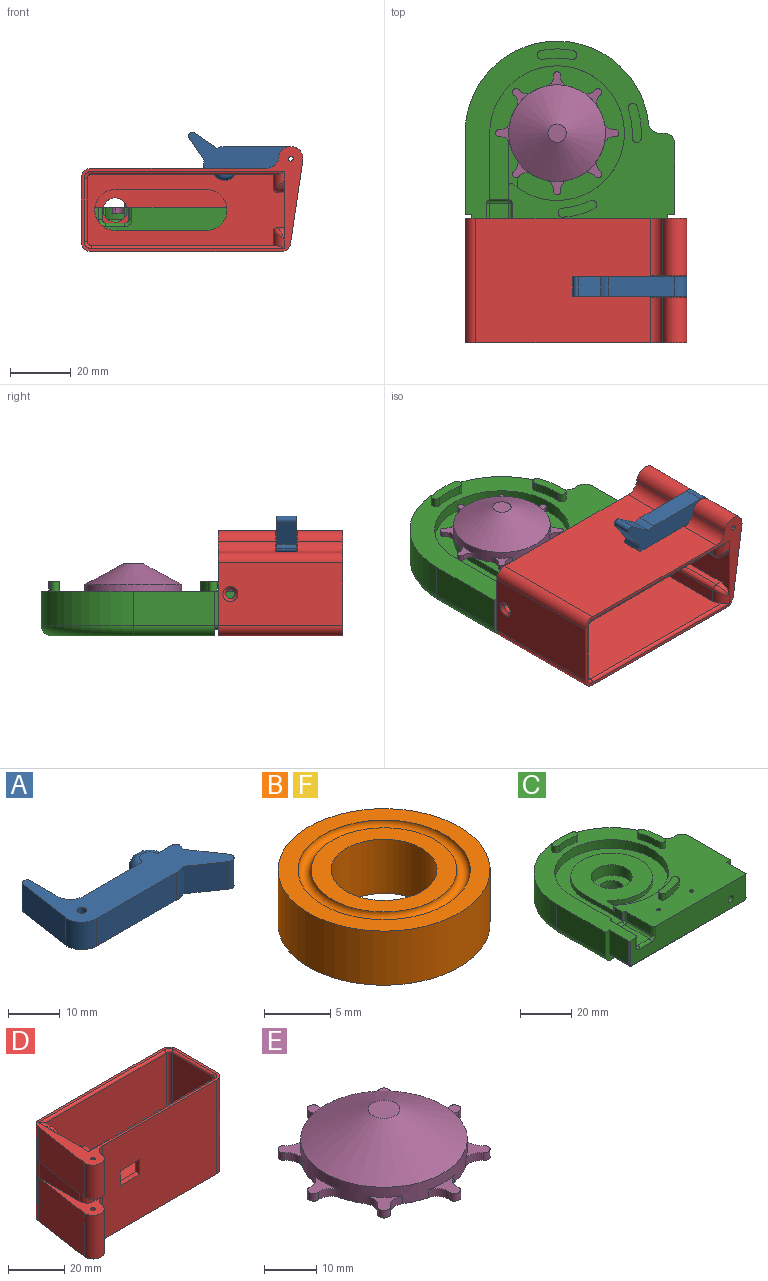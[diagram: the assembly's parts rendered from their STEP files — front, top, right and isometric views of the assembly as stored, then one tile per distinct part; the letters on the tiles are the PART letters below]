
ASSEMBLY  parts=6 mates=9
PART A: 20 faces, bbox 37.6x23.8x6.5 mm
  f0: plane 37.63x23.77mm, normal (0,0,1), area 292.8mm2, adj f1,f2,f3,f4,f5,f6,f7,f8
  f1: plane 13.58x6.5mm, normal (-0.99,0.15,0), area 89.3mm2, adj f0,f2,f12,f17
  f2: cylinder r=4mm len=6.5mm, axis (0,0,-1), area 44.7mm2, adj f0,f1,f3,f12
  f3: plane 21.75x6.5mm, normal (0,-1,0), area 141.4mm2, adj f0,f2,f4,f12
  f4: cylinder r=7.13mm len=6.5mm, axis (0,0,-1), area 17.3mm2, adj f0,f3,f5,f12
  f5: plane 7.29x6.5mm, normal (-0.57,-0.82,0), area 57.5mm2, adj f0,f4,f6,f12
  f6: cylinder r=1.27mm len=6.5mm, axis (0,0,-1), area 22.9mm2, adj f0,f5,f7,f12
  f7: plane 7.29x6.5mm, normal (0.82,0.57,0), area 57.5mm2, adj f0,f6,f8,f12
  f8: cylinder r=7.13mm len=6.5mm, axis (0,0,-1), area 9.7mm2, adj f0,f7,f9,f12
  f9: cylinder r=1mm len=6.5mm, axis (0,0,-1), area 11.3mm2, adj f0,f8,f10,f12
  f10: plane 6.5x4.05mm, normal (0,1,0), area 15mm2, adj f0,f9,f11,f12,f18,f19
  f11: cylinder r=4mm len=8mm, axis (0,0,-1), area 31.4mm2, adj f10,f14,f18,f19
  f12: plane 37.63x23.77mm, normal (0,0,-1), area 292.8mm2, adj f1,f2,f3,f4,f5,f6,f7,f8
  f13: cylinder r=0.95mm len=6.5mm, axis (0,0,-1), area 38.9mm2, adj f0,f12
  f14: plane 16.25x6.5mm, normal (0,1,0), area 94.3mm2, adj f0,f11,f12,f16,f18,f19
  f15: plane 6.88x6.5mm, normal (1,0,0), area 44.7mm2, adj f0,f12,f16,f17
  f16: cylinder r=3.5mm len=6.5mm, axis (0,0,-1), area 39.1mm2, adj f0,f12,f14,f15
  f17: cylinder r=1mm len=6.5mm, axis (0,0,1), area 19.5mm2, adj f0,f1,f12,f15
  f18: torus R=2mm, axis (0,0,1), area 32.3mm2, adj f0,f10,f11,f14
  f19: torus R=2mm, axis (0,0,1), area 32.3mm2, adj f10,f11,f12,f14
PART B: 8 faces, bbox 16x16x5.7 mm
  f0: plane 16x16mm, normal (0,0,1), area 68.3mm2, adj f2,f4
  f1: plane 16x16mm, normal (0,0,-1), area 68.3mm2, adj f2,f3
  f2: cylinder r=8mm len=16mm, axis (0,0,-1), area 251.3mm2, adj f0,f1
  f3: torus R=6mm, axis (0,0,-1), area 59.2mm2, adj f1,f7
  f4: torus R=6mm, axis (0,0,-1), area 59.2mm2, adj f0,f5
  f5: plane 11x11mm, normal (0,0,1), area 44.8mm2, adj f4,f6
  f6: cylinder r=4mm len=8mm, axis (0,0,-1), area 125.7mm2, adj f5,f7
  f7: plane 11x11mm, normal (0,0,-1), area 44.8mm2, adj f3,f6
PART C: 75 faces, bbox 71.5x70.6x17.8 mm
  f0: plane 69x68.06mm, normal (0,0,1), area 2131.6mm2, adj f2,f3,f5,f6,f10,f16,f19,f20
  f1: plane 62x53.56mm, normal (0,0,-1), area 2566mm2, adj f15,f21,f24,f26,f27,f28,f42
  f2: plane 23.28x11.25mm, normal (1,0,0), area 261.9mm2, adj f0,f21,f22,f42
  f3: plane 11.25x1.62mm, normal (0,1,0), area 18.2mm2, adj f0,f22,f24,f25
  f4: plane 44.31x44.31mm, normal (0,0,1), area 787.6mm2, adj f5,f6,f8,f9,f10,f17,f18,f51
  f5: plane 21.96x4.13mm, normal (-1,0,0), area 56mm2, adj f0,f4,f8,f11,f16,f48
  f6: plane 21.96x4.13mm, normal (1,0,0), area 90.6mm2, adj f0,f4,f10,f50
  f7: cylinder r=4.5mm len=9mm, axis (0,0,1), area 77.8mm2, adj f13,f14
  f8: cylinder r=15.91mm len=31.81mm, axis (0,0,1), area 187.3mm2, adj f4,f5,f11,f18
  f9: plane 6.16x2.13mm, normal (1,0,0), area 13.1mm2, adj f4,f11,f17,f18
  f10: cylinder r=22.16mm len=44.31mm, axis (0,0,1), area 491.4mm2, adj f0,f4,f6,f11,f16,f17
  f11: plane 34.01x31.81mm, normal (0,0,1), area 625.2mm2, adj f5,f8,f9,f10,f12,f16,f17,f18
  f12: cylinder r=8mm len=16mm, axis (0,0,1), area 251.3mm2, adj f11,f13
  f13: plane 16x16mm, normal (0,0,1), area 137.4mm2, adj f7,f12
  f14: plane 16x16mm, normal (0,0,-1), area 137.4mm2, adj f7,f15
  f15: cylinder r=8mm len=16mm, axis (0,0,-1), area 251.3mm2, adj f1,f14
  f16: cylinder r=0.8mm len=2mm, axis (0,0,1), area 3.7mm2, adj f0,f5,f10,f11
  f17: cylinder r=0.8mm len=2.13mm, axis (0,0,1), area 1.6mm2, adj f4,f9,f10,f11
  f18: cylinder r=0.8mm len=2.13mm, axis (0,0,1), area 4.1mm2, adj f4,f8,f9,f11
  f19: plane 26.78x11.25mm, normal (-1,0,0), area 301.3mm2, adj f0,f20,f27,f42
  f20: cylinder r=30.28mm len=60.4mm, axis (0,0,1), area 1034.9mm2, adj f0,f19,f25,f28
  f21: cylinder r=3.5mm len=23.28mm, axis (0,1,0), area 128mm2, adj f1,f2,f23,f42
  f22: cylinder r=3.5mm len=11.25mm, axis (0,0,-1), area 61.9mm2, adj f0,f2,f3,f23
  f23: sphere r=3.5mm, area 19.2mm2, adj f21,f22,f24
  f24: cylinder r=3.5mm len=3.5mm, axis (1,0,0), area 8.9mm2, adj f1,f3,f23,f26
  f25: cylinder r=3.5mm len=11.25mm, axis (0,0,1), area 57.8mm2, adj f0,f3,f20,f26
  f26: torus R=7mm, axis (0,0,1), area 38.5mm2, adj f1,f24,f25,f28
  f27: cylinder r=3.5mm len=26.78mm, axis (0,1,0), area 147.2mm2, adj f1,f19,f28,f42
  f28: torus R=26.78mm, axis (0,0,1), area 484.5mm2, adj f1,f20,f26,f27
  f29: plane 63.7x12.1mm, normal (0,-1,0), area 694.9mm2, adj f0,f36,f37,f38,f39,f40,f41,f53
  f30: plane 11.25x10.6mm, normal (1,0,0), area 119.3mm2, adj f0,f34,f41,f42
  f31: plane 11.25x10.6mm, normal (-1,0,0), area 119.3mm2, adj f0,f32,f37,f42
  f32: cylinder r=1.25mm len=10.6mm, axis (0,1,0), area 20.8mm2, adj f31,f33,f38,f42
  f33: plane 62x10.6mm, normal (0,0,-1), area 653.2mm2, adj f32,f34,f39,f42,f43,f44
  f34: cylinder r=1.25mm len=10.6mm, axis (0,1,0), area 20.8mm2, adj f30,f33,f40,f42
  f35: plane 3x3mm, normal (0,-1,0), area 7.1mm2, adj f36
  f36: cylinder r=1.5mm len=12mm, axis (0,-1,0), area 113.1mm2, adj f29,f35
  f37: cylinder r=0.4mm len=11.25mm, axis (0,0,1), area 7.1mm2, adj f0,f29,f31,f38
  f38: torus R=0.85mm, axis (0,1,0), area 1.1mm2, adj f29,f32,f37,f39
  f39: cylinder r=0.4mm len=62mm, axis (-1,0,0), area 39mm2, adj f29,f33,f38,f40
  f40: torus R=0.85mm, axis (0,1,0), area 1.1mm2, adj f29,f34,f39,f41
  f41: cylinder r=0.4mm len=11.25mm, axis (0,0,-1), area 7.1mm2, adj f0,f29,f30,f40
  f42: plane 69x14.75mm, normal (0,-1,0), area 206.9mm2, adj f0,f1,f2,f19,f21,f27,f30,f31
  f43: cylinder r=0.79mm len=12.5mm, axis (0,0,-1), area 62.3mm2, adj f0,f33
  f44: cylinder r=0.79mm len=12.5mm, axis (0,0,-1), area 62.3mm2, adj f0,f33
  f45: plane 13.48x4.13mm, normal (1,0,0), area 55.6mm2, adj f0,f50,f56,f59
  f46: plane 13.48x6.25mm, normal (0,0,1), area 84.2mm2, adj f51,f52,f56,f57
  f47: plane 13.48x4.13mm, normal (-1,0,0), area 55.6mm2, adj f0,f48,f52,f53
  f48: cylinder r=1.18mm len=4.13mm, axis (0,0,-1), area 7.6mm2, adj f0,f5,f47,f49
  f49: sphere r=1.18mm, area 2.2mm2, adj f48,f51,f52
  f50: cylinder r=1.18mm len=4.13mm, axis (0,0,1), area 7.6mm2, adj f0,f6,f45,f54
  f51: cylinder r=1.18mm len=6.25mm, axis (-1,0,0), area 11.5mm2, adj f4,f46,f49,f54
  f52: cylinder r=1.18mm len=13.48mm, axis (0,-1,0), area 24.9mm2, adj f46,f47,f49,f55
  f53: cylinder r=1.18mm len=4.13mm, axis (0,0,1), area 7.6mm2, adj f0,f29,f47,f55
  f54: sphere r=1.18mm, area 2.2mm2, adj f50,f51,f56
  f55: torus R=2.35mm, axis (0,1,0), area 4.6mm2, adj f29,f52,f53,f57
  f56: cylinder r=1.18mm len=13.48mm, axis (0,1,0), area 24.9mm2, adj f45,f46,f54,f58
  f57: cylinder r=1.18mm len=6.25mm, axis (1,0,0), area 11.5mm2, adj f29,f46,f55,f58
  f58: torus R=2.35mm, axis (0,1,0), area 4.6mm2, adj f29,f56,f57,f59
  f59: cylinder r=1.18mm len=4.13mm, axis (0,0,-1), area 7.6mm2, adj f0,f29,f45,f58
  f60: cylinder r=24.72mm len=9.43mm, axis (0,0,-1), area 28.5mm2, adj f0,f61,f63,f64
  f61: cylinder r=1.5mm len=3mm, axis (0,0,-1), area 14.1mm2, adj f0,f60,f62,f64
  f62: cylinder r=27.72mm len=10.57mm, axis (0,0,-1), area 31.9mm2, adj f0,f61,f63,f64
  f63: cylinder r=1.5mm len=3mm, axis (0,0,-1), area 14.1mm2, adj f0,f60,f62,f64
  f64: plane 13x3.48mm, normal (0,0,1), area 37.3mm2, adj f60,f61,f62,f63
  f65: cylinder r=24.72mm len=9.35mm, axis (0,0,-1), area 28.5mm2, adj f0,f66,f68,f69
  f66: cylinder r=1.5mm len=3mm, axis (0,0,-1), area 14.1mm2, adj f0,f65,f67,f69
  f67: cylinder r=27.72mm len=10.48mm, axis (0,0,-1), area 31.9mm2, adj f0,f66,f68,f69
  f68: cylinder r=1.5mm len=3mm, axis (0,0,-1), area 14.1mm2, adj f0,f65,f67,f69
  f69: plane 12.91x4.35mm, normal (0,0,1), area 37.3mm2, adj f65,f66,f67,f68
  f70: cylinder r=24.72mm len=9.11mm, axis (0,0,-1), area 28.5mm2, adj f0,f71,f73,f74
  f71: cylinder r=1.5mm len=3mm, axis (0,0,-1), area 14.1mm2, adj f0,f70,f72,f74
  f72: cylinder r=27.72mm len=10.21mm, axis (0,0,-1), area 31.9mm2, adj f0,f71,f73,f74
  f73: cylinder r=1.5mm len=3mm, axis (0,0,-1), area 14.1mm2, adj f0,f70,f72,f74
  f74: plane 12.66x5.59mm, normal (0,0,1), area 37.3mm2, adj f70,f71,f72,f73
PART D: 56 faces, bbox 73x34.6x41 mm
  f0: plane 27.06x19mm, normal (-0.99,0.15,0), area 519.7mm2, adj f2,f6,f47,f55
  f1: cylinder r=4mm len=19mm, axis (0,0,-1), area 111.1mm2, adj f2,f5,f47,f55
  f2: cylinder r=4mm len=19mm, axis (0,0,-1), area 241.6mm2, adj f0,f1,f47,f55
  f3: cylinder r=0.79mm len=19mm, axis (0,0,-1), area 94.8mm2, adj f47,f55
  f4: cylinder r=0.79mm len=15mm, axis (0,0,-1), area 74.8mm2, adj f25,f54
  f5: plane 62x41mm, normal (0,-1,0), area 2325.6mm2, adj f1,f9,f10,f25,f31,f32,f33,f34
  f6: cylinder r=3.5mm len=41mm, axis (0,0,-1), area 208mm2, adj f0,f8,f13,f25,f47,f52,f54,f55
  f7: plane 60.95x29mm, normal (0,1,0), area 1668.8mm2, adj f21,f22,f26,f31,f32,f33,f34,f37
  f8: plane 20.5x7mm, normal (-1,0,0), area 143.5mm2, adj f6,f9,f54,f55
  f9: cylinder r=3.5mm len=7mm, axis (0,0,-1), area 38.5mm2, adj f5,f8,f54,f55
  f10: cylinder r=3.5mm len=41mm, axis (0,0,-1), area 225.4mm2, adj f5,f11,f25,f47
  f11: plane 41x20.5mm, normal (1,0,0), area 821.6mm2, adj f10,f12,f25,f47,f53
  f12: cylinder r=3.5mm len=41mm, axis (0,0,-1), area 225.4mm2, adj f11,f13,f25,f47
  f13: plane 62x41mm, normal (0,1,0), area 2542mm2, adj f6,f12,f25,f47
  f14: plane 30x19mm, normal (1,0,0), area 351mm2, adj f15,f24,f25,f26,f35,f38
  f15: plane 26.25x2.25mm, normal (0,-1,0), area 59.1mm2, adj f14,f16,f26,f38
  f16: cylinder r=1.5mm len=26.25mm, axis (0,0,-1), area 61.9mm2, adj f15,f17,f26,f39
  f17: plane 26.25x4.5mm, normal (1,0,0), area 118.1mm2, adj f16,f18,f26,f40
  f18: plane 60.95x29mm, normal (0,-1,0), area 1733.8mm2, adj f17,f19,f26,f40,f45
  f19: cylinder r=1.5mm len=29mm, axis (0,0,-1), area 68.3mm2, adj f18,f20,f26,f44
  f20: plane 29x20.5mm, normal (-1,0,0), area 594.5mm2, adj f19,f21,f26,f43
  f21: cylinder r=1.5mm len=29mm, axis (0,0,-1), area 68.3mm2, adj f7,f20,f26,f42
  f22: plane 26.25x4.5mm, normal (1,0,0), area 118.1mm2, adj f7,f23,f26,f37
  f23: cylinder r=1.5mm len=26.25mm, axis (0,0,-1), area 61.9mm2, adj f22,f24,f26,f36
  f24: plane 26.25x2.25mm, normal (0,1,0), area 59.1mm2, adj f14,f23,f26,f35
  f25: plane 73x34.63mm, normal (0,0,1), area 303.6mm2, adj f4,f5,f6,f10,f11,f12,f13,f14
  f26: plane 65x23.5mm, normal (0,0,1), area 934.4mm2, adj f7,f14,f15,f16,f17,f18,f19,f20
  f27: cylinder r=6.75mm len=13.5mm, axis (0,0,1), area 63.6mm2, adj f26,f28,f30,f46
  f28: plane 30x3mm, normal (0,-1,0), area 90mm2, adj f26,f27,f29,f46
  f29: cylinder r=6.75mm len=13.5mm, axis (0,0,1), area 63.6mm2, adj f26,f28,f30,f46
  f30: plane 30x3mm, normal (0,1,0), area 90mm2, adj f26,f27,f29,f46
  f31: plane 10x2mm, normal (0,0,1), area 20mm2, adj f5,f7,f32,f33
  f32: plane 6.5x2mm, normal (1,0,0), area 13mm2, adj f5,f7,f31,f34
  f33: plane 6.5x2mm, normal (-1,0,0), area 13mm2, adj f5,f7,f31,f34
  f34: plane 10x2mm, normal (0,0,-1), area 20mm2, adj f5,f7,f32,f33
  f35: cylinder r=3.75mm len=3.75mm, axis (1,0,0), area 8.4mm2, adj f14,f24,f36
  f36: bspline ~4.43x3.75mm, area 9.4mm2, adj f23,f35,f37
  f37: cylinder r=3.75mm len=5.5mm, axis (0,-1,0), area 22.8mm2, adj f7,f22,f25,f36,f41
  f38: cylinder r=3.75mm len=3.75mm, axis (-1,0,0), area 8.4mm2, adj f14,f15,f39
  f39: bspline ~4.43x3.75mm, area 9.4mm2, adj f16,f38,f40
  f40: cylinder r=3.75mm len=5.5mm, axis (0,-1,0), area 22.8mm2, adj f17,f18,f25,f39,f45
  f41: cylinder r=1mm len=63.5mm, axis (1,0,0), area 97.6mm2, adj f7,f25,f37,f42
  f42: torus R=2.5mm, axis (0,0,1), area 4.6mm2, adj f21,f25,f41,f43
  f43: cylinder r=1mm len=20.5mm, axis (0,1,0), area 32.2mm2, adj f20,f25,f42,f44
  f44: torus R=2.5mm, axis (0,0,1), area 4.6mm2, adj f19,f25,f43,f45
  f45: cylinder r=1mm len=63.5mm, axis (-1,0,0), area 97.6mm2, adj f18,f25,f40,f44
  f46: plane 43.5x13.5mm, normal (0,0,1), area 497.9mm2, adj f27,f28,f29,f30,f48
  f47: plane 73x34.63mm, normal (0,0,-1), area 1933.7mm2, adj f0,f1,f2,f3,f5,f6,f10,f11
  f48: cylinder r=4mm len=8mm, axis (0,0,1), area 194.3mm2, adj f46,f47,f49
  f49: cylinder r=1.45mm len=6.52mm, axis (1,0,0), area 58.2mm2, adj f48,f53
  f50: cylinder r=4mm len=15mm, axis (0,0,-1), area 87.7mm2, adj f5,f25,f51,f54
  f51: cylinder r=4mm len=15mm, axis (0,0,-1), area 190.8mm2, adj f25,f50,f52,f54
  f52: plane 27.06x15mm, normal (-0.99,0.15,0), area 410.3mm2, adj f6,f25,f51,f54
  f53: cone r=1.45mm half-angle=45deg, axis (1,0,0), area 17.3mm2, adj f11,f49
  f54: plane 31.64x11.95mm, normal (0,0,-1), area 96.9mm2, adj f4,f5,f6,f8,f9,f50,f51,f52
  f55: plane 31.64x11.95mm, normal (0,0,1), area 96.9mm2, adj f0,f1,f2,f3,f5,f6,f8,f9
PART E: 42 faces, bbox 40.5x40.5x11.1 mm
  f0: plane 40.46x40.46mm, normal (0,0,-1), area 843.4mm2, adj f9,f10,f11,f12,f13,f14,f15,f16
  f1: plane 6.55x5.5mm, normal (-1,0,0), area 36mm2, adj f38,f39,f41
  f2: plane 6.24x6.24mm, normal (0,0,1), area 12.4mm2, adj f9,f16,f17,f18
  f3: plane 7.18x4.74mm, normal (0,0,1), area 12.4mm2, adj f9,f19,f20,f21
  f4: plane 6.24x6.24mm, normal (0,0,1), area 12.4mm2, adj f9,f22,f23,f24
  f5: plane 7.18x4.74mm, normal (0,0,1), area 12.4mm2, adj f9,f25,f26,f27
  f6: plane 6.24x6.24mm, normal (0,0,1), area 12.4mm2, adj f9,f28,f29,f30
  f7: plane 7.18x4.74mm, normal (0,0,1), area 12.4mm2, adj f9,f31,f32,f33
  f8: plane 7.18x4.74mm, normal (0,0,1), area 12.4mm2, adj f13,f14,f15,f35
  f9: cylinder r=15.91mm len=31.81mm, axis (0,0,-1), area 291.1mm2, adj f0,f2,f3,f4,f5,f6,f7,f10
  f10: cylinder r=3.12mm len=4.1mm, axis (0,0,-1), area 8.2mm2, adj f0,f9,f11,f34
  f11: cylinder r=1.2mm len=2.14mm, axis (0,0,-1), area 7.3mm2, adj f0,f10,f12,f34
  f12: cylinder r=3.12mm len=4.1mm, axis (0,0,-1), area 8.2mm2, adj f0,f9,f11,f34
  f13: cylinder r=3.12mm len=3.4mm, axis (0,0,-1), area 8.2mm2, adj f0,f8,f9,f14
  f14: cylinder r=1.2mm len=2.4mm, axis (0,0,-1), area 7.3mm2, adj f0,f8,f13,f15
  f15: cylinder r=3.12mm len=3.4mm, axis (0,0,-1), area 8.2mm2, adj f0,f8,f9,f14
  f16: cylinder r=3.12mm len=4.1mm, axis (0,0,-1), area 8.2mm2, adj f0,f2,f9,f17
  f17: cylinder r=1.2mm len=2.14mm, axis (0,0,-1), area 7.3mm2, adj f0,f2,f16,f18
  f18: cylinder r=3.12mm len=4.1mm, axis (0,0,-1), area 8.2mm2, adj f0,f2,f9,f17
  f19: cylinder r=3.12mm len=3.4mm, axis (0,0,-1), area 8.2mm2, adj f0,f3,f9,f20
  f20: cylinder r=1.2mm len=2.4mm, axis (0,0,-1), area 7.3mm2, adj f0,f3,f19,f21
  f21: cylinder r=3.12mm len=3.4mm, axis (0,0,-1), area 8.2mm2, adj f0,f3,f9,f20
  f22: cylinder r=3.12mm len=4.1mm, axis (0,0,-1), area 8.2mm2, adj f0,f4,f9,f23
  f23: cylinder r=1.2mm len=2.14mm, axis (0,0,-1), area 7.3mm2, adj f0,f4,f22,f24
  f24: cylinder r=3.12mm len=4.1mm, axis (0,0,-1), area 8.2mm2, adj f0,f4,f9,f23
  f25: cylinder r=3.12mm len=3.4mm, axis (0,0,-1), area 8.2mm2, adj f0,f5,f9,f26
  f26: cylinder r=1.2mm len=2.4mm, axis (0,0,-1), area 7.3mm2, adj f0,f5,f25,f27
  f27: cylinder r=3.12mm len=3.4mm, axis (0,0,-1), area 8.2mm2, adj f0,f5,f9,f26
  f28: cylinder r=3.12mm len=4.1mm, axis (0,0,-1), area 8.2mm2, adj f0,f6,f9,f29
  f29: cylinder r=1.2mm len=2.14mm, axis (0,0,-1), area 7.3mm2, adj f0,f6,f28,f30
  f30: cylinder r=3.12mm len=4.1mm, axis (0,0,-1), area 8.2mm2, adj f0,f6,f9,f29
  f31: cylinder r=3.12mm len=3.4mm, axis (0,0,-1), area 8.2mm2, adj f0,f7,f9,f32
  f32: cylinder r=1.2mm len=2.4mm, axis (0,0,-1), area 7.3mm2, adj f0,f7,f31,f33
  f33: cylinder r=3.12mm len=3.4mm, axis (0,0,-1), area 8.2mm2, adj f0,f7,f9,f32
  f34: plane 6.24x6.24mm, normal (0,0,1), area 12.4mm2, adj f9,f10,f11,f12
  f35: extruded ~7.18x2.33mm, area 16.8mm2, adj f8,f9,f37
  f36: plane 6x6mm, normal (0,0,1), area 28.3mm2, adj f37
  f37: cone r=3mm half-angle=61.5deg, axis (0,0,-1), area 872.1mm2, adj f9,f35,f36
  f38: cylinder r=4mm len=8mm, axis (0,0,-1), area 139.7mm2, adj f0,f1,f39,f40
  f39: plane 8x6.3mm, normal (0,0,-1), area 42.5mm2, adj f1,f38
  f40: extruded ~6.55x2.5mm, area 19.2mm2, adj f0,f38,f41
  f41: plane 6.55x1.7mm, normal (0,0,-1), area 7.8mm2, adj f1,f40
PART F: same geometry as B
PLACE A rot(axis=(0,-0.71,0.71),180deg) t=(-168.87,-134.81,30.95)mm
PLACE B t=(-173.09,-98.85,24.95)mm
PLACE C t=(-173.09,-98.85,17.2)mm
PLACE D rot(axis=(0,-0.71,0.71),180deg) t=(-168.87,-134.81,30.95)mm
PLACE E t=(-173.09,-98.85,17.2)mm
PLACE F t=(-173.09,-98.85,17.2)mm
MATE planar B.f2 <-> C.f12  axis (0,0,-1) through (-173.09,-98.85,24.95)mm
MATE cylindrical E.f38 <-> B.f2  axis (0,0,-1) through (-173.09,-98.85,29.95)mm
MATE planar A.f0 <-> D.f34  axis (0,-1,0) through (-147.21,-152.56,47.57)mm
MATE cylindrical B.f6 <-> C.f12  axis (0,0,1) through (-173.09,-98.85,29.95)mm
MATE parallel A.f14 <-> D.f5  axis (0,0,-1) through (-145.13,-149.31,44.7)mm
MATE planar E.f0 <-> C.f11  axis (0,0,-1) through (-164.67,-112.35,29.95)mm
MATE cylindrical A.f2 <-> D.f2  axis (0,1,0) through (-134.37,-149.31,47.84)mm
MATE cylindrical F.f2 <-> C.f15  axis (0,0,-1) through (-173.09,-98.85,19.7)mm
MATE planar F.f2 <-> C.f15  axis (0,0,1) through (-173.09,-98.85,22.2)mm
